# Revit family: Plymold-Cascade-Chair+
name_source: partatom
category: Furniture
units: mm (PartAtom-declared; Revit-internal decimal feet)

## family parameters
Always vertical = Yes
Cut with Voids When Loaded = No
OmniClass Number = 23.40.20.00
OmniClass Title = General Furniture and Specialties
Render Appearance Source = Family Geometry
Room Calculation Point = No
Shared = No
Work Plane-Based = No

## types (1)
- 6781
    Assembly Code = E2020200
    BACK MATERIAL = PLY - Vinyl - Lite Gray
    BASE MATERIAL = PLY - Wood Mahogany
    Default Elevation = 0"
    Depth = 21"
    Description = Chair - 19.5"W x 21"D x 31.5"H
    FRAME MATERIAL = PLY - Silver
    GLIDES MATERIAL = PLY - Plastic Black
    Height = 31 1/2"
    Keynote = 12500
    Manufacturer = Plymold Inc.
    Model = 6781
    Product Documentation Link = https://plymold.com
    Revit File Built By = https://servex-us.com
    SEAT MATERIAL = PLY - Vinyl - Lite Gray
    Sustainability = https://plymold.com
    Type Comments = Cascade
    URL = https://plymold.com
    Width = 19 1/2"

## geometry (parser evidence)
native form markers: Sweep x6
no freeform markers — native parametric forms only
